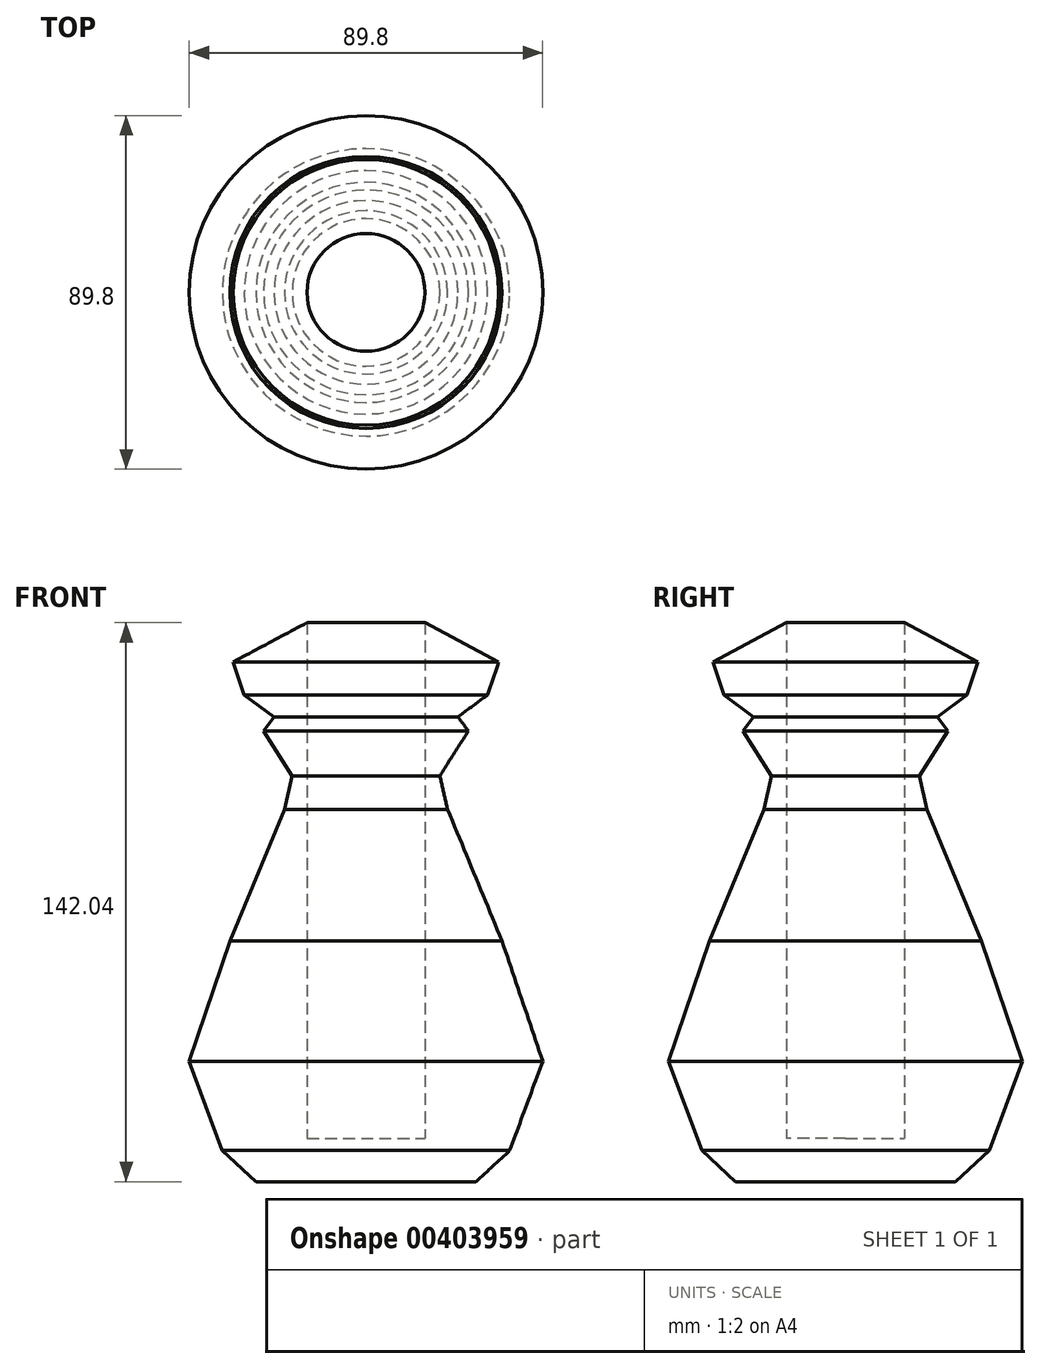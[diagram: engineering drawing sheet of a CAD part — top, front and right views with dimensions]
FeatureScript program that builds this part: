
annotation { "Feature Type Name" : "Feature", "Feature Type Description" : "" }
export const myFeature = defineFeature(function(context is Context, id is Id, definition is map)
    precondition{}
    {
        {
            var Q0;
            Q0=qCreatedBy(makeId("Front.planeOp"),FACE);
            var sketch = newSketch(context, id + "F0", { "sketchPlane" : qUnion([Q0])});
            skLineSegment(sketch, "E0", {"start": v(0, 70.4) * mm, "end": v(-33.72, 52.47) * mm});
            skLineSegment(sketch, "E1", {"start": v(-33.72, 52.47) * mm, "end": v(-30.92, 44.08) * mm});
            skLineSegment(sketch, "E2", {"start": v(-30.92, 44.08) * mm, "end": v(-23.36, 38.49) * mm});
            skLineSegment(sketch, "E3", {"start": v(-23.36, 38.49) * mm, "end": v(-26.01, 34.89) * mm});
            skLineSegment(sketch, "E4", {"start": v(-26.01, 34.89) * mm, "end": v(-18.75, 23.52) * mm});
            skLineSegment(sketch, "E5", {"start": v(-18.75, 23.52) * mm, "end": v(-20.72, 14.97) * mm});
            skLineSegment(sketch, "E6", {"start": v(-20.72, 14.97) * mm, "end": v(-34.54, -18.42) * mm});
            skLineSegment(sketch, "E7", {"start": v(-34.54, -18.42) * mm, "end": v(-44.9, -49.01) * mm});
            skLineSegment(sketch, "E8", {"start": v(-44.9, -49.01) * mm, "end": v(-36.51, -71.71) * mm});
            skLineSegment(sketch, "E9", {"start": v(-36.51, -71.71) * mm, "end": v(-27.96, -79.6) * mm});
            skLineSegment(sketch, "E10", {"start": v(-27.96, -79.6) * mm, "end": v(0, -79.6) * mm});
            skLineSegment(sketch, "E11", {"start": v(0, 70.4) * mm, "end": v(0, -79.6) * mm});
            skSolve(sketch);
        }
        {
            var Q0;
            Q0=makeQuery(id+"F0.imprint","IMPRINT",FACE,{"disambiguationData":[TD([[makeQuery(id+"F0.imprint","IMPRINT",EDGE,{"derivedFrom":sQuery(id+"F0.wireOp",EDGE,"E0")}),1.0]])]});
            var Q1;
            Q1=sQuery(id+"F0.wireOp",EDGE,"E11");
            revolve(context, id + "F1", {"entities" : qUnion([Q0]), "axis" : qUnion([Q1]), "revolveType" : RevolveType.FULL});
        }
        {
            var Q0;
            Q0=qCreatedBy(makeId("Top.planeOp"),FACE);
            var sketch = newSketch(context, id + "F2", { "sketchPlane" : qUnion([Q0])});
            skCircle(sketch, "E12", {"center": v(0, 0) * mm, "radius": 14.97 * mm});
            skSolve(sketch);
        }
        {
            var Q0;
            Q0 = qSketchRegion(id + "F2", true);
            var Q1;
            Q1=sQuery(id+"F2.wireOp",EDGE,"E12");
            extrude(context, id + "F3", {"entities" : qUnion([Q0]), "operationType" : NewBodyOperationType.REMOVE, "surfaceEntities" : qUnion([Q1]), "depth" : 88.4 * mm});
        }
        {
            var Q0;
            Q0 = qSketchRegion(id + "F2", true);
            extrude(context, id + "F4", {"entities" : qUnion([Q0]), "operationType" : NewBodyOperationType.REMOVE, "oppositeDirection" : true, "depth" : 68.58 * mm});
        }
    });
